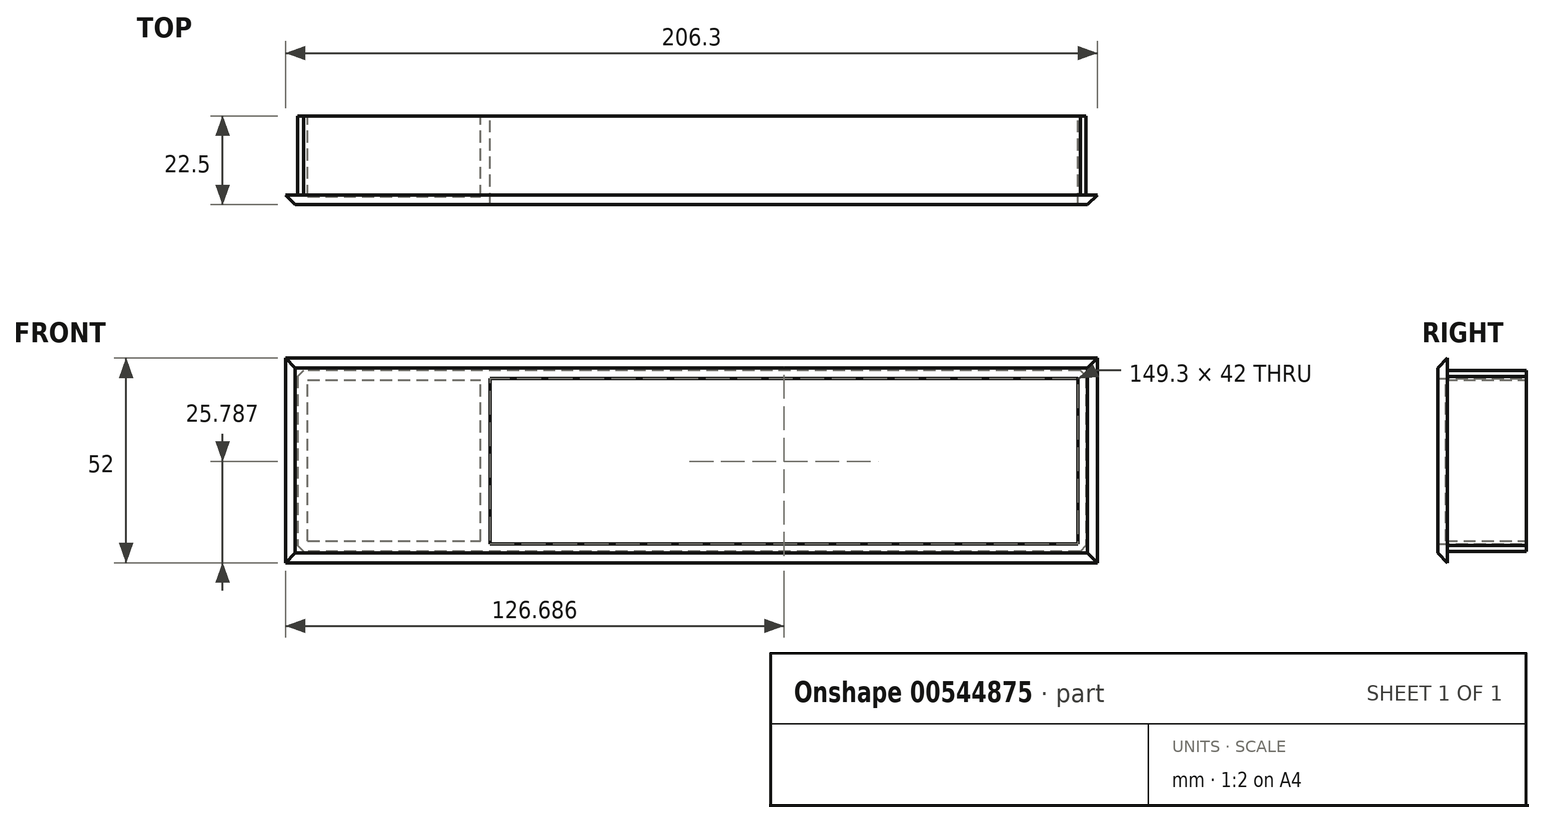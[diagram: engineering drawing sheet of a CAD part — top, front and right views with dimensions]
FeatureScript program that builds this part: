
annotation { "Feature Type Name" : "Feature", "Feature Type Description" : "" }
export const myFeature = defineFeature(function(context is Context, id is Id, definition is map)
    precondition{}
    {
        {
            var Q0;
            Q0=qCreatedBy(makeId("Front.planeOp"),FACE);
            var sketch = newSketch(context, id + "F0", { "sketchPlane" : qUnion([Q0])});
            skLineSegment(sketch, "E0.bottom", {"start": v(-21.18, 44.16) * mm, "end": v(185.12, 44.16) * mm});
            skLineSegment(sketch, "E0.top", {"start": v(-21.18, -7.84) * mm, "end": v(185.12, -7.84) * mm});
            skLineSegment(sketch, "E0.left", {"start": v(-21.18, 44.16) * mm, "end": v(-21.18, -7.84) * mm});
            skLineSegment(sketch, "E0.right", {"start": v(185.12, 44.16) * mm, "end": v(185.12, -7.84) * mm});
            skSolve(sketch);
        }
        {
            var Q0;
            Q0=makeQuery(id+"F0.imprint","IMPRINT",FACE,{"disambiguationData":[TD([[makeQuery(id+"F0.imprint","IMPRINT",EDGE,{"derivedFrom":sQuery(id+"F0.wireOp",EDGE,"E0.bottom")}),-1.0]])]});
            extrude(context, id + "F1", {"entities" : qUnion([Q0]), "depth" : 2.5 * mm, "offsetDistance" : 25 * mm});
        }
        {
            var Q0;
            Q0=makeQuery(id+"F1.opExtrude","CAP_EDGE",EDGE,{"disambiguationData":[OSD([sQuery(id+"F0.wireOp",EDGE,"E0.bottom")])],"isStart":false});
            var Q1;
            Q1=makeQuery(id+"F1.opExtrude","CAP_EDGE",EDGE,{"disambiguationData":[OSD([sQuery(id+"F0.wireOp",EDGE,"E0.top")])],"isStart":false});
            var Q2;
            Q2=makeQuery(id+"F1.opExtrude","CAP_EDGE",EDGE,{"disambiguationData":[OSD([sQuery(id+"F0.wireOp",EDGE,"E0.right")])],"isStart":false});
            var Q3;
            Q3=makeQuery(id+"F1.opExtrude","CAP_EDGE",EDGE,{"disambiguationData":[OSD([sQuery(id+"F0.wireOp",EDGE,"E0.left")])],"isStart":false});
            chamfer(context, id + "F2", {"entities" : qUnion([Q0, Q1, Q2, Q3]), "width" : 2.5 * mm, "tangentPropagation" : true});
        }
        {
            var Q0;
            Q0=makeQuery(id+"F1.opExtrude","CAP_FACE",FACE,{"disambiguationData":[OSD([sQuery(id+"F0.wireOp",EDGE,"E0.bottom"),sQuery(id+"F0.wireOp",EDGE,"E0.top"),sQuery(id+"F0.wireOp",EDGE,"E0.left"),sQuery(id+"F0.wireOp",EDGE,"E0.right")])],"isStart":true});
            var sketch = newSketch(context, id + "F3", { "sketchPlane" : qUnion([Q0])});
            skLineSegment(sketch, "E1.bottom", {"start": v(-182.23, 41.06) * mm, "end": v(18.07, 41.06) * mm});
            skLineSegment(sketch, "E1.top", {"start": v(-182.23, -4.94) * mm, "end": v(18.07, -4.94) * mm});
            skLineSegment(sketch, "E1.left", {"start": v(-182.23, 41.06) * mm, "end": v(-182.23, -4.94) * mm});
            skLineSegment(sketch, "E1.right", {"start": v(18.07, 41.06) * mm, "end": v(18.07, -4.94) * mm});
            skSolve(sketch);
        }
        {
            var Q0;
            Q0 = qSketchRegion(id + "F3", true);
            extrude(context, id + "F4", {"entities" : qUnion([Q0]), "operationType" : NewBodyOperationType.ADD, "depth" : 20 * mm, "offsetDistance" : 25 * mm});
        }
        {
            var Q0;
            Q0=makeQuery(id+"F4.opExtrude","CAP_FACE",FACE,{"disambiguationData":[OSD([sQuery(id+"F3.wireOp",EDGE,"E1.bottom"),sQuery(id+"F3.wireOp",EDGE,"E1.top"),sQuery(id+"F3.wireOp",EDGE,"E1.left"),sQuery(id+"F3.wireOp",EDGE,"E1.right")])],"isStart":false});
            var sketch = newSketch(context, id + "F5", { "sketchPlane" : qUnion([Q0])});
            skLineSegment(sketch, "E2.bottom", {"start": v(-180.16, 38.95) * mm, "end": v(16.14, 38.95) * mm});
            skLineSegment(sketch, "E2.top", {"start": v(-180.16, -3.05) * mm, "end": v(16.14, -3.05) * mm});
            skLineSegment(sketch, "E2.left", {"start": v(-180.16, 38.95) * mm, "end": v(-180.16, -3.05) * mm});
            skLineSegment(sketch, "E2.right", {"start": v(16.14, 38.95) * mm, "end": v(16.14, -3.05) * mm});
            skSolve(sketch);
        }
        {
            var Q0;
            Q0=makeQuery(id+"F5.imprint","IMPRINT",FACE,{"disambiguationData":[TD([[makeQuery(id+"F5.imprint","IMPRINT",EDGE,{"derivedFrom":sQuery(id+"F5.wireOp",EDGE,"E2.bottom")}),-1.0]])]});
            extrude(context, id + "F6", {"entities" : qUnion([Q0]), "operationType" : NewBodyOperationType.REMOVE, "oppositeDirection" : true, "depth" : 25 * mm, "offsetDistance" : 25 * mm});
        }
        {
            var Q0;
            Q0=makeQuery(id+"F4.opExtrude","SWEPT_EDGE",EDGE,{"disambiguationData":[OSD([sQuery(id+"F3.wireOp",EDGE,"E1.bottom"),sQuery(id+"F3.wireOp",EDGE,"E1.left")])]});
            var Q1;
            Q1=makeQuery(id+"F4.opExtrude","SWEPT_EDGE",EDGE,{"disambiguationData":[OSD([sQuery(id+"F3.wireOp",EDGE,"E1.top"),sQuery(id+"F3.wireOp",EDGE,"E1.left")])]});
            var Q2;
            Q2=makeQuery(id+"F4.opExtrude","SWEPT_EDGE",EDGE,{"disambiguationData":[OSD([sQuery(id+"F3.wireOp",EDGE,"E1.bottom"),sQuery(id+"F3.wireOp",EDGE,"E1.right")])]});
            var Q3;
            Q3=makeQuery(id+"F4.opExtrude","SWEPT_EDGE",EDGE,{"disambiguationData":[OSD([sQuery(id+"F3.wireOp",EDGE,"E1.top"),sQuery(id+"F3.wireOp",EDGE,"E1.right")])]});
            chamfer(context, id + "F7", {"entities" : qUnion([Q0, Q1, Q2, Q3]), "width" : 1.5 * mm, "tangentPropagation" : true});
        }
        {
            var Q0;
            Q0=makeQuery(id+"F6.boolean.opBoolean","COPY",FACE,{"derivedFrom":makeQuery(id+"F6.opExtrude","SWEPT_FACE",FACE,{"disambiguationData":[OSD([sQuery(id+"F5.wireOp",EDGE,"E2.right")])]})});
            extrude(context, id + "F8", {"entities" : qUnion([Q0]), "operationType" : NewBodyOperationType.ADD, "depth" : 47 * mm, "offsetDistance" : 25 * mm});
        }
        {
            var Q0;
            Q0=makeQuery(id+"F8.boolean.opBoolean","MERGE",FACE,{"derivedFrom":[makeQuery(id+"F4.opExtrude","CAP_FACE",FACE,{"disambiguationData":[OSD([sQuery(id+"F3.wireOp",EDGE,"E1.bottom"),sQuery(id+"F3.wireOp",EDGE,"E1.top"),sQuery(id+"F3.wireOp",EDGE,"E1.left"),sQuery(id+"F3.wireOp",EDGE,"E1.right")])],"isStart":false}),makeQuery(id+"F8.opExtrude","SWEPT_FACE",FACE,{"disambiguationData":[OSD([sQuery(id+"F5.wireOp",EDGE,"E2.right")])]})]});
            var sketch = newSketch(context, id + "F9", { "sketchPlane" : qUnion([Q0])});
            skLineSegment(sketch, "E3.bottom", {"start": v(15.53, -2.33) * mm, "end": v(-28.32, -2.33) * mm});
            skLineSegment(sketch, "E3.top", {"start": v(15.53, 38.55) * mm, "end": v(-28.32, 38.55) * mm});
            skLineSegment(sketch, "E3.left", {"start": v(15.53, -2.33) * mm, "end": v(15.53, 38.55) * mm});
            skLineSegment(sketch, "E3.right", {"start": v(-28.32, -2.33) * mm, "end": v(-28.32, 38.55) * mm});
            skSolve(sketch);
        }
        {
            var Q0;
            Q0=makeQuery(id+"F9.imprint","IMPRINT",FACE,{"disambiguationData":[TD([[makeQuery(id+"F9.imprint","IMPRINT",EDGE,{"derivedFrom":sQuery(id+"F9.wireOp",EDGE,"E3.bottom")}),-1.0]])]});
            extrude(context, id + "F10", {"entities" : qUnion([Q0]), "operationType" : NewBodyOperationType.REMOVE, "oppositeDirection" : true, "depth" : 20.5 * mm, "offsetDistance" : 25 * mm});
        }
    });
